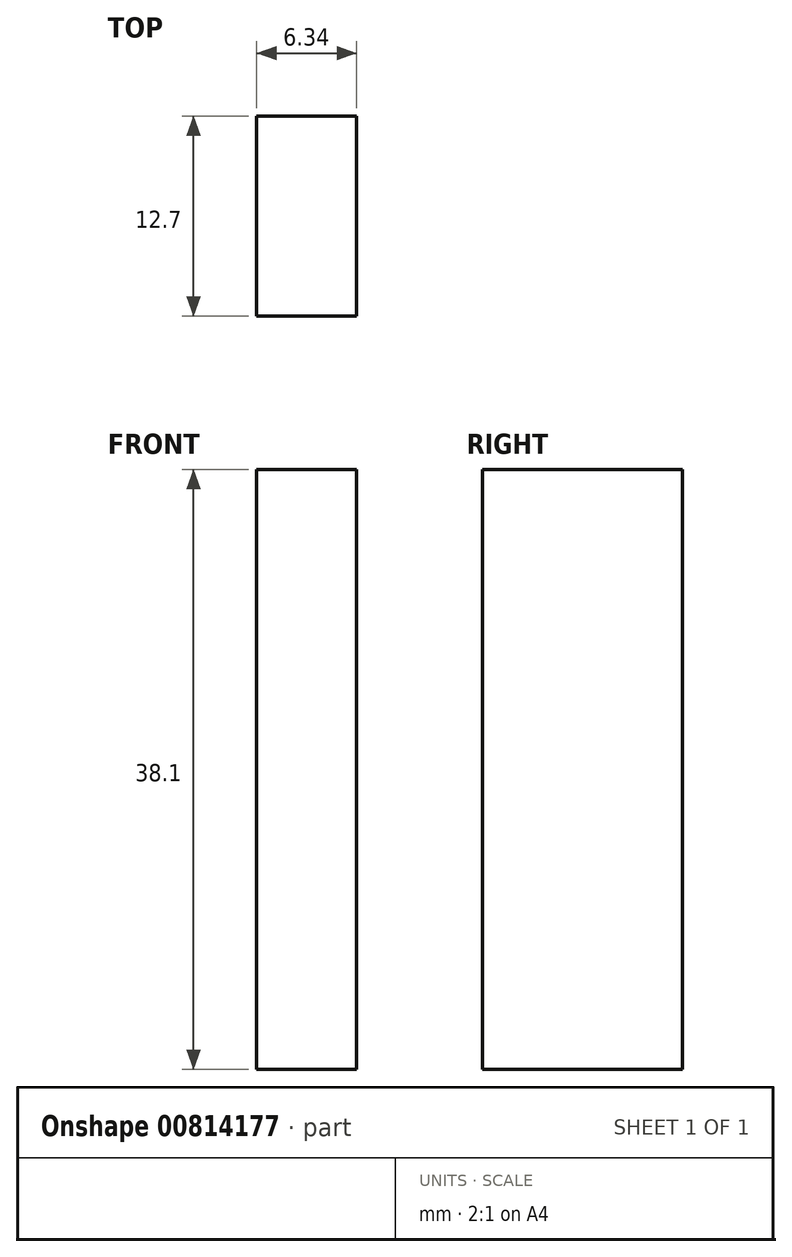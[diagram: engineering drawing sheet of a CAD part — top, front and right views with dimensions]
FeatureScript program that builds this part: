
annotation { "Feature Type Name" : "Feature", "Feature Type Description" : "" }
export const myFeature = defineFeature(function(context is Context, id is Id, definition is map)
    precondition{}
    {
        {
            var Q0;
            Q0=qCreatedBy(makeId("Top.planeOp"),FACE);
            var sketch = newSketch(context, id + "F0", { "sketchPlane" : qUnion([Q0])});
            skLineSegment(sketch, "E0.bottom", {"start": v(3.18, 6.35) * mm, "end": v(-3.17, 6.35) * mm});
            skLineSegment(sketch, "E0.top", {"start": v(3.17, -6.35) * mm, "end": v(-3.18, -6.35) * mm});
            skLineSegment(sketch, "E0.left", {"start": v(3.18, 6.35) * mm, "end": v(3.17, -6.35) * mm});
            skLineSegment(sketch, "E0.right", {"start": v(-3.17, 6.35) * mm, "end": v(-3.18, -6.35) * mm});
            skPoint(sketch, "E0.middle", {"position": v(0, 0) * mm});
            skSolve(sketch);
        }
        {
            var Q0;
            Q0=makeQuery(id+"F0.imprint","IMPRINT",FACE,{"disambiguationData":[TD([[makeQuery(id+"F0.imprint","IMPRINT",EDGE,{"derivedFrom":sQuery(id+"F0.wireOp",EDGE,"E0.bottom")}),1.0]])]});
            extrude(context, id + "F1", {"entities" : qUnion([Q0]), "depth" : 38.1 * mm, "offsetDistance" : 25.4 * mm});
        }
    });
